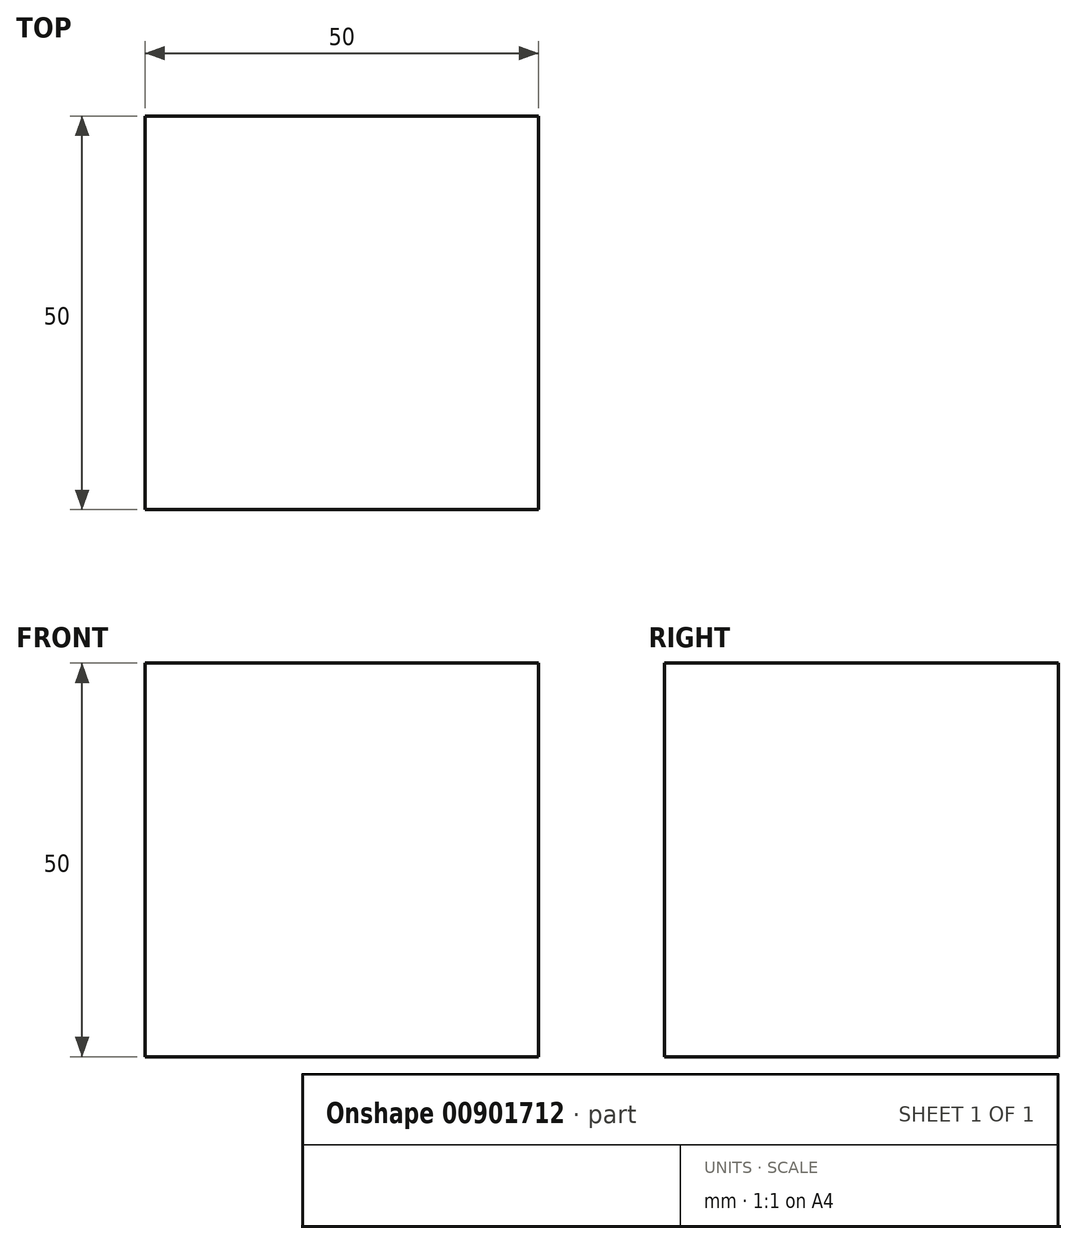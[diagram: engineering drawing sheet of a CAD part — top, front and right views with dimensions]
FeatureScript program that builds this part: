
annotation { "Feature Type Name" : "Feature", "Feature Type Description" : "" }
export const myFeature = defineFeature(function(context is Context, id is Id, definition is map)
    precondition{}
    {
        {
            var Q0;
            Q0=qCreatedBy(makeId("Front.planeOp"),FACE);
            var sketch = newSketch(context, id + "F0", { "sketchPlane" : qUnion([Q0])});
            skLineSegment(sketch, "E0.bottom", {"start": v(25, -25) * mm, "end": v(-25, -25) * mm});
            skLineSegment(sketch, "E0.top", {"start": v(25, 25) * mm, "end": v(-25, 25) * mm});
            skLineSegment(sketch, "E0.left", {"start": v(25, -25) * mm, "end": v(25, 25) * mm});
            skLineSegment(sketch, "E0.right", {"start": v(-25, -25) * mm, "end": v(-25, 25) * mm});
            skPoint(sketch, "E0.middle", {"position": v(0, 0) * mm});
            skSolve(sketch);
        }
        {
            var Q0;
            Q0 = qSketchRegion(id + "F0", true);
            extrude(context, id + "F1", {"entities" : qUnion([Q0]), "endBound" : BoundingType.SYMMETRIC, "depth" : 50 * mm, "offsetDistance" : 25 * mm});
        }
    });
